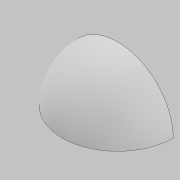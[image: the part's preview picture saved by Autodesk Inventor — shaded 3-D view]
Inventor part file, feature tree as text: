
AUTODESK INVENTOR PART (.ipt)
format: ipt  version: 2021 (Build 250183000, 183)  size: 120,832 bytes
history: native  units: mm
features: other x3, revolve x1, sketch x1
ambient origin geometry x8: Origin, YZ Plane, XZ Plane, XY Plane, X Axis, Y Axis, Z Axis, Center Point
bodies: Body1 (feature_tree)
feature tree (5):
  revolve  "Revolution1"  [1 undecoded]
  other  "midPlane"
  sketch  "Sketch1"  dims[d0=10.0mm d1=1000.0mm d2=0.0mm d3=0.0mm d6=180.0deg d9=0.872665mm d10=0.872665mm]
  other  "tangentPlane1"
  other  "tangentPlane2"
note: 1 required parameter value undecoded (feature->parameter linkage not recoverable at this tier; creation-order binding heuristic only, values carry confidence <= 0.55)
